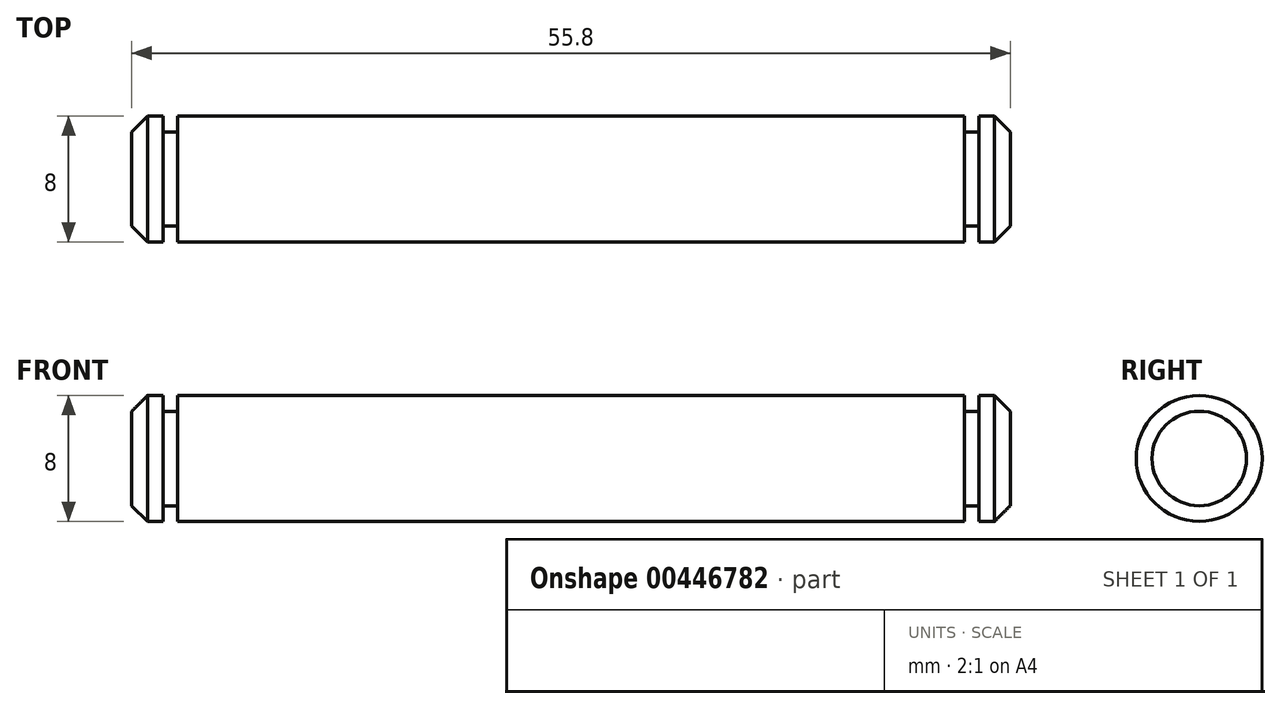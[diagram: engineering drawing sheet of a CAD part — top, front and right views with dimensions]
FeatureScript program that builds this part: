
annotation { "Feature Type Name" : "Feature", "Feature Type Description" : "" }
export const myFeature = defineFeature(function(context is Context, id is Id, definition is map)
    precondition{}
    {
        {
            var Q0;
            Q0=qCreatedBy(makeId("Front.planeOp"),FACE);
            var sketch = newSketch(context, id + "F0", { "sketchPlane" : qUnion([Q0])});
            skLineSegment(sketch, "E0", {"start": v(-5.98, 0) * mm, "end": v(61.5, 0) * mm, "construction": true});
            skLineSegment(sketch, "E1", {"start": v(0, 0) * mm, "end": v(0, 4) * mm});
            skLineSegment(sketch, "E2", {"start": v(0, 4) * mm, "end": v(2, 4) * mm});
            skLineSegment(sketch, "E3", {"start": v(2, 4) * mm, "end": v(2, 3) * mm});
            skLineSegment(sketch, "E4", {"start": v(2, 3) * mm, "end": v(2.9, 3) * mm});
            skLineSegment(sketch, "E5", {"start": v(2.9, 3) * mm, "end": v(2.9, 4) * mm});
            skLineSegment(sketch, "E6", {"start": v(2.9, 4) * mm, "end": v(52.9, 4) * mm});
            skLineSegment(sketch, "E7", {"start": v(52.9, 4) * mm, "end": v(52.9, 3) * mm});
            skLineSegment(sketch, "E8", {"start": v(52.9, 3) * mm, "end": v(53.8, 3) * mm});
            skLineSegment(sketch, "E9", {"start": v(53.8, 3) * mm, "end": v(53.8, 4) * mm});
            skLineSegment(sketch, "E10", {"start": v(53.8, 4) * mm, "end": v(55.8, 4) * mm});
            skLineSegment(sketch, "E11", {"start": v(55.8, 4) * mm, "end": v(55.8, 0) * mm});
            skLineSegment(sketch, "E12", {"start": v(55.8, 0) * mm, "end": v(0, 0) * mm});
            skSolve(sketch);
        }
        {
            var Q0;
            Q0 = qSketchRegion(id + "F0", true);
            var Q1;
            Q1=sQuery(id+"F0.wireOp",EDGE,"E0");
            revolve(context, id + "F1", {"entities" : qUnion([Q0]), "axis" : qUnion([Q1]), "revolveType" : RevolveType.FULL});
        }
        {
            var Q0;
            Q0=makeQuery(id+"F1.opRevolve","SWEPT_EDGE",EDGE,{"disambiguationData":[OSD([sQuery(id+"F0.wireOp",EDGE,"E10"),sQuery(id+"F0.wireOp",EDGE,"E11")])]});
            var Q1;
            Q1=makeQuery(id+"F1.opRevolve","SWEPT_EDGE",EDGE,{"disambiguationData":[OSD([sQuery(id+"F0.wireOp",EDGE,"E1"),sQuery(id+"F0.wireOp",EDGE,"E2")])]});
            chamfer(context, id + "F2", {"entities" : qUnion([Q0, Q1]), "width" : 1 * mm, "tangentPropagation" : true});
        }
    });
